# Revit family: LH-Series Bar Joist-Side
name_source: partatom
category: Detail Items
revit_build: Autodesk Revit Architecture 2012 (Build: 20110210_1515)
units: mm (PartAtom-declared; Revit-internal decimal feet)

## types (80) — shared parameters
Bearing Height = 0' - 2 1/2"
Bearing Right = 0' - 4"
Bottom Angle Leg = 0' - 1 1/4"
Lower Leg Ext. = 0' - 1"
Lower Leg Off = 1' - 9"
Top Angle Leg = 0' - 1 1/4"

## per-type parameters (varying)
| type | Depth | Keynote | Wt |
| 18LH02 | 1' - 6" | 05 21 00.C1 | 10 |
| 18LH03 | 1' - 6" | 05 21 00.C2 | 11 |
| 18LH04 | 1' - 6" | 05 21 00.C3 | 12 |
| 18LH05 | 1' - 6" | 05 21 00.C4 | 15 |
| 18LH06 | 1' - 6" | 05 21 00.C5 | 15 |
| 18LH07 | 1' - 6" | 05 21 00.C6 | 17 |
| 18LH08 | 1' - 6" | 05 21 00.C7 | 19 |
| 18LH09 | 1' - 6" | 05 21 00.C8 | 21 |
| 20LH02 | 1' - 8" | 05 21 00.C9 | 10 |
| 20LH03 | 1' - 8" | 05 21 00.C10 | 11 |
| 20LH04 | 1' - 8" | 05 21 00.C11 | 12 |
| 20LH05 | 1' - 8" | 05 21 00.C12 | 14 |
| 20LH06 | 1' - 8" | 05 21 00.C13 | 15 |
| 20LH07 | 1' - 8" | 05 21 00.C14 | 17 |
| 20LH08 | 1' - 8" | 05 21 00.C15 | 19 |
| 20LH09 | 1' - 8" | 05 21 00.C16 | 21 |
| 20LH10 | 1' - 8" | 05 21 00.C17 | 23 |
| 24LH03 | 2' - 0" | 05 21 00.C18 | 11 |
| 24LH04 | 2' - 0" | 05 21 00.C19 | 12 |
| 24LH05 | 2' - 0" | 05 21 00.C20 | 13 |
| 24LH06 | 2' - 0" | 05 21 00.C21 | 16 |
| 24LH07 | 2' - 0" | 05 21 00.C22 | 17 |
| 24LH08 | 2' - 0" | 05 21 00.C23 | 18 |
| 24LH09 | 2' - 0" | 05 21 00.C24 | 21 |
| 24LH10 | 2' - 0" | 05 21 00.C25 | 23 |
| 24LH11 | 2' - 0" | 05 21 00.C26 | 25 |
| 28LH05 | 2' - 4" | 05 21 00.C27 | 13 |
| 28LH06 | 2' - 4" | 05 21 00.C28 | 16 |
| 28LH07 | 2' - 4" | 05 21 00.C29 | 17 |
| 28LH08 | 2' - 4" | 05 21 00.C30 | 18 |
| 28LH09 | 2' - 4" | 05 21 00.C31 | 21 |
| 28LH10 | 2' - 4" | 05 21 00.C32 | 23 |
| 28LH11 | 2' - 4" | 05 21 00.C33 | 25 |
| 28LH12 | 2' - 4" | 05 21 00.C34 | 27 |
| 28LH13 | 2' - 4" | 05 21 00.C35 | 30 |
| 32LH06 | 2' - 8" | 05 21 00.C36 | 14 |
| 32LH07 | 2' - 8" | 05 21 00.C37 | 16 |
| 32LH08 | 2' - 8" | 05 21 00.C38 | 17 |
| 32LH09 | 2' - 8" | 05 21 00.C39 | 21 |
| 32LH10 | 2' - 8" | 05 21 00.C40 | 21 |
| 32LH11 | 2' - 8" | 05 21 00.C41 | 24 |
| 32LH12 | 2' - 8" | 05 21 00.C42 | 27 |
| 32LH13 | 2' - 8" | 05 21 00.C43 | 30 |
| 32LH14 | 2' - 8" | 05 21 00.C44 | 33 |
| 32LH15 | 2' - 8" | 05 21 00.C45 | 35 |
| 36LH07 | 3' - 0" | 05 21 00.C46 | 16 |
| 36LH08 | 3' - 0" | 05 21 00.C47 | 18 |
| 36LH09 | 3' - 0" | 05 21 00.C48 | 21 |
| 36LH10 | 3' - 0" | 05 21 00.C49 | 21 |
| 36LH11 | 3' - 0" | 05 21 00.C50 | 23 |
| 36LH12 | 3' - 0" | 05 21 00.C51 | 25 |
| 36LH13 | 3' - 0" | 05 21 00.C52 | 30 |
| 36LH14 | 3' - 0" | 05 21 00.C53 | 36 |
| 36LH15 | 3' - 0" | 05 21 00.C54 | 36 |
| 40LH08 | 3' - 4" | 05 21 00.C55 | 16 |
| 40LH09 | 3' - 4" | 05 21 00.C56 | 21 |
| 40LH10 | 3' - 4" | 05 21 00.C57 | 21 |
| 40LH11 | 3' - 4" | 05 21 00.C58 | 22 |
| 40LH12 | 3' - 4" | 05 21 00.C59 | 25 |
| 40LH13 | 3' - 4" | 05 21 00.C60 | 30 |
| 40LH14 | 3' - 4" | 05 21 00.C61 | 35 |
| 40LH15 | 3' - 4" | 05 21 00.C62 | 36 |
| 40LH16 | 3' - 4" | 05 21 00.C63 | 42 |
| 44LH09 | 3' - 8" | 05 21 00.C64 | 19 |
| 44LH10 | 3' - 8" | 05 21 00.C65 | 21 |
| 44LH11 | 3' - 8" | 05 21 00.C66 | 22 |
| 44LH12 | 3' - 8" | 05 21 00.C67 | 25 |
| 44LH13 | 3' - 8" | 05 21 00.C68 | 30 |
| 44LH14 | 3' - 8" | 05 21 00.C69 | 31 |
| 44LH15 | 3' - 8" | 05 21 00.C70 | 36 |
| 44LH16 | 3' - 8" | 05 21 00.C71 | 42 |
| 44LH17 | 3' - 8" | 05 21 00.C72 | 47 |
| 48LH10 | 4' - 0" | 05 21 00.C73 | 21 |
| 48LH11 | 4' - 0" | 05 21 00.C74 | 22 |
| 48LH12 | 4' - 0" | 05 21 00.C75 | 25 |
| 48LH13 | 4' - 0" | 05 21 00.C76 | 29 |
| 48LH14 | 4' - 0" | 05 21 00.C77 | 32 |
| 48LH15 | 4' - 0" | 05 21 00.C78 | 36 |
| 48LH16 | 4' - 0" | 05 21 00.C79 | 42 |
| 48LH17 | 4' - 0" | 05 21 00.C80 | 47 |
